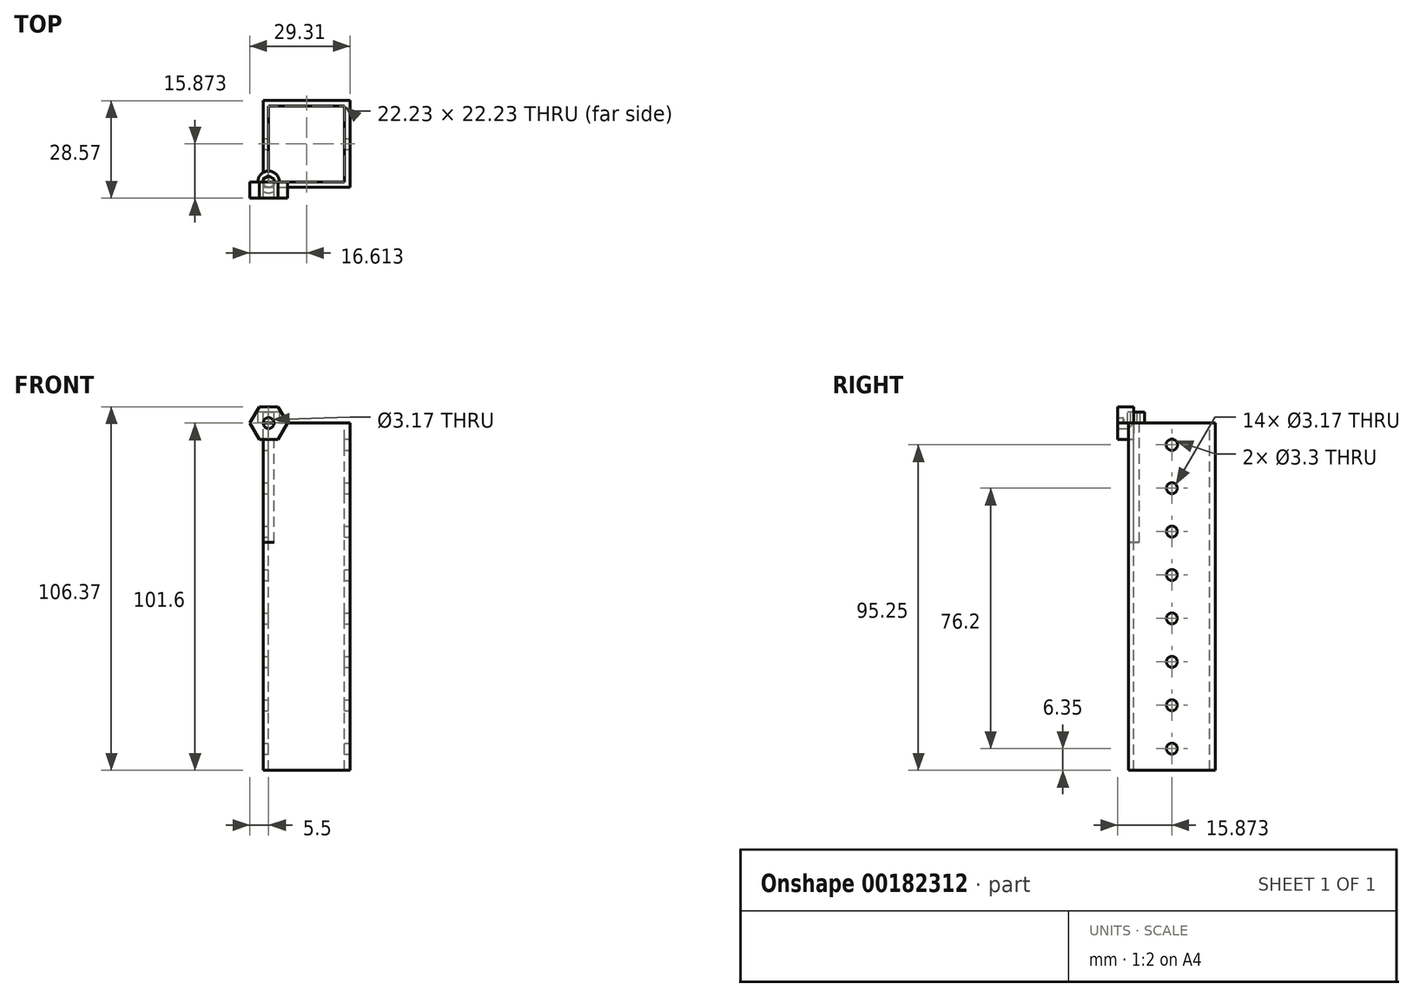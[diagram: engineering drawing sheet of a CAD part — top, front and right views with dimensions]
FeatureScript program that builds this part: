
annotation { "Feature Type Name" : "Feature", "Feature Type Description" : "" }
export const myFeature = defineFeature(function(context is Context, id is Id, definition is map)
    precondition{}
    {
        {
            var Q0;
            Q0=qCreatedBy(makeId("Front.planeOp"),FACE);
            var sketch = newSketch(context, id + "F0", { "sketchPlane" : qUnion([Q0])});
            skCircle(sketch, "E0.cCircle", {"center": v(0, 0) * mm, "radius": 4.76 * mm, "construction": true});
            skLineSegment(sketch, "E0.0", {"start": v(5.5, 0) * mm, "end": v(2.76, -4.76) * mm});
            skLineSegment(sketch, "E0.1", {"start": v(2.76, -4.76) * mm, "end": v(-2.74, -4.77) * mm});
            skLineSegment(sketch, "E0.2", {"start": v(-2.74, -4.77) * mm, "end": v(-5.5, 0) * mm});
            skLineSegment(sketch, "E0.3", {"start": v(-5.5, 0) * mm, "end": v(-2.76, 4.76) * mm});
            skLineSegment(sketch, "E0.4", {"start": v(-2.76, 4.76) * mm, "end": v(2.74, 4.77) * mm});
            skLineSegment(sketch, "E0.5", {"start": v(2.74, 4.77) * mm, "end": v(5.5, 0) * mm});
            skPoint(sketch, "E0.0.midPoint", {"position": v(4.13, -2.38) * mm});
            skSolve(sketch);
        }
        {
            var Q0;
            Q0=makeQuery(id+"F0.imprint","IMPRINT",FACE,{"disambiguationData":[TD([[makeQuery(id+"F0.imprint","IMPRINT",EDGE,{"derivedFrom":sQuery(id+"F0.wireOp",EDGE,"E0.0")}),-1.0]])]});
            var sketch = newSketch(context, id + "F1", { "sketchPlane" : qUnion([Q0])});
            skCircle(sketch, "E1", {"center": v(0, 0) * mm, "radius": 1.58 * mm});
            skSolve(sketch);
        }
        {
            var Q0;
            Q0=makeQuery(id+"F0.imprint","IMPRINT",FACE,{"disambiguationData":[TD([[makeQuery(id+"F0.imprint","IMPRINT",EDGE,{"derivedFrom":sQuery(id+"F0.wireOp",EDGE,"E0.0")}),-1.0]])]});
            extrude(context, id + "F2", {"entities" : qUnion([Q0]), "depth" : 4.76 * mm});
        }
        {
            var Q0;
            Q0 = qSketchRegion(id + "F1", true);
            extrude(context, id + "F3", {"entities" : qUnion([Q0]), "operationType" : NewBodyOperationType.REMOVE, "depth" : 4.76 * mm});
        }
        {
            var Q0;
            Q0=qCreatedBy(makeId("Top.planeOp"),FACE);
            var sketch = newSketch(context, id + "F4", { "sketchPlane" : qUnion([Q0])});
            skCircle(sketch, "E2", {"center": v(0, 0) * mm, "radius": 3.18 * mm});
            skSolve(sketch);
        }
        {
            var Q0;
            Q0=makeQuery(id+"F4.imprint","IMPRINT",FACE,{"disambiguationData":[TD([[makeQuery(id+"F4.imprint","IMPRINT",EDGE,{"derivedFrom":sQuery(id+"F4.wireOp",EDGE,"E2")}),1.0]])]});
            extrude(context, id + "F5", {"entities" : qUnion([Q0]), "depth" : 3.17 * mm});
        }
        {
            var Q0;
            Q0=makeQuery(id+"F5.opExtrude","CAP_FACE",FACE,{"disambiguationData":[OSD([sQuery(id+"F4.wireOp",EDGE,"E2")])],"isStart":true});
            var sketch = newSketch(context, id + "F6", { "sketchPlane" : qUnion([Q0])});
            skCircle(sketch, "E3", {"center": v(0, 0) * mm, "radius": 1.59 * mm});
            skSolve(sketch);
        }
        {
            var Q0;
            Q0=makeQuery(id+"F6.imprint","IMPRINT",FACE,{"disambiguationData":[TD([[makeQuery(id+"F6.imprint","IMPRINT",EDGE,{"derivedFrom":sQuery(id+"F6.wireOp",EDGE,"E3")}),1.0]])]});
            extrude(context, id + "F7", {"entities" : qUnion([Q0]), "operationType" : NewBodyOperationType.ADD, "depth" : 34.92 * mm});
        }
        {
            var Q0;
            Q0=makeQuery(id+"F5.opExtrude","CAP_FACE",FACE,{"disambiguationData":[OSD([sQuery(id+"F4.wireOp",EDGE,"E2")])],"isStart":false});
            var sketch = newSketch(context, id + "F8", { "sketchPlane" : qUnion([Q0])});
            skCircle(sketch, "E4.cCircle", {"center": v(0, 0) * mm, "radius": 1.59 * mm, "construction": true});
            skLineSegment(sketch, "E4.0", {"start": v(-1.59, -0.92) * mm, "end": v(-1.59, 0.92) * mm});
            skLineSegment(sketch, "E4.1", {"start": v(-1.59, 0.92) * mm, "end": v(0, 1.83) * mm});
            skLineSegment(sketch, "E4.2", {"start": v(0, 1.83) * mm, "end": v(1.59, 0.92) * mm});
            skLineSegment(sketch, "E4.3", {"start": v(1.59, 0.92) * mm, "end": v(1.59, -0.92) * mm});
            skLineSegment(sketch, "E4.4", {"start": v(1.59, -0.92) * mm, "end": v(0, -1.83) * mm});
            skLineSegment(sketch, "E4.5", {"start": v(0, -1.83) * mm, "end": v(-1.59, -0.92) * mm});
            skPoint(sketch, "E4.0.midPoint", {"position": v(-1.59, 0) * mm});
            skSolve(sketch);
        }
        {
            var Q0;
            Q0=makeQuery(id+"F8.imprint","IMPRINT",FACE,{"disambiguationData":[TD([[makeQuery(id+"F8.imprint","IMPRINT",EDGE,{"derivedFrom":sQuery(id+"F8.wireOp",EDGE,"E4.0")}),-1.0]])]});
            extrude(context, id + "F9", {"entities" : qUnion([Q0]), "operationType" : NewBodyOperationType.REMOVE, "oppositeDirection" : true, "depth" : 3.15 * mm});
        }
        {
            var Q0;
            Q0=qCreatedBy(makeId("Top.planeOp"),FACE);
            var sketch = newSketch(context, id + "F10", { "sketchPlane" : qUnion([Q0])});
            skLineSegment(sketch, "E5.bottom", {"start": v(0, 0) * mm, "end": v(22.23, 0) * mm});
            skLineSegment(sketch, "E5.top", {"start": v(0, 22.23) * mm, "end": v(22.22, 22.23) * mm});
            skLineSegment(sketch, "E5.left", {"start": v(0, 0) * mm, "end": v(0, 22.23) * mm});
            skLineSegment(sketch, "E5.right", {"start": v(22.23, 0) * mm, "end": v(22.23, 22.23) * mm});
            skSolve(sketch);
        }
        {
            var Q0;
            Q0=qCreatedBy(makeId("Top.planeOp"),FACE);
            var sketch = newSketch(context, id + "F11", { "sketchPlane" : qUnion([Q0])});
            skLineSegment(sketch, "E6.bottom", {"start": v(-1.59, -1.59) * mm, "end": v(23.81, -1.59) * mm});
            skLineSegment(sketch, "E6.top", {"start": v(-1.59, 23.81) * mm, "end": v(23.81, 23.81) * mm});
            skLineSegment(sketch, "E6.left", {"start": v(-1.59, -1.59) * mm, "end": v(-1.59, 23.81) * mm});
            skLineSegment(sketch, "E6.right", {"start": v(23.81, -1.59) * mm, "end": v(23.81, 23.81) * mm});
            skSolve(sketch);
        }
        {
            var Q0;
            Q0=makeQuery(id+"F11.imprint","IMPRINT",FACE,{"disambiguationData":[TD([[makeQuery(id+"F11.imprint","IMPRINT",EDGE,{"derivedFrom":sQuery(id+"F11.wireOp",EDGE,"E6.bottom")}),1.0]])]});
            extrude(context, id + "F12", {"entities" : qUnion([Q0]), "oppositeDirection" : true, "depth" : 101.6 * mm});
        }
        {
            var Q0;
            Q0=makeQuery(id+"F10.imprint","IMPRINT",FACE,{"disambiguationData":[TD([[makeQuery(id+"F10.imprint","IMPRINT",EDGE,{"derivedFrom":sQuery(id+"F10.wireOp",EDGE,"E5.bottom")}),1.0]])]});
            extrude(context, id + "F13", {"entities" : qUnion([Q0]), "operationType" : NewBodyOperationType.REMOVE, "oppositeDirection" : true, "depth" : 101.6 * mm});
        }
        {
            var Q0;
            Q0=makeQuery(id+"F12.opExtrude","SWEPT_FACE",FACE,{"disambiguationData":[OSD([sQuery(id+"F11.wireOp",EDGE,"E6.right")])]});
            var sketch = newSketch(context, id + "F14", { "sketchPlane" : qUnion([Q0])});
            skCircle(sketch, "E7", {"center": v(11.11, -6.35) * mm, "radius": 1.65 * mm});
            skSolve(sketch);
        }
        {
            var Q0;
            Q0=makeQuery(id+"F14.imprint","IMPRINT",FACE,{"disambiguationData":[TD([[makeQuery(id+"F14.imprint","IMPRINT",EDGE,{"derivedFrom":sQuery(id+"F14.wireOp",EDGE,"E7")}),-1.0]])]});
            var sketch = newSketch(context, id + "F15", { "sketchPlane" : qUnion([Q0])});
            skCircle(sketch, "E8", {"center": v(11.11, -19.05) * mm, "radius": 1.59 * mm});
            skSolve(sketch);
        }
        {
            var Q0;
            Q0=makeQuery(id+"F14.imprint","IMPRINT",FACE,{"disambiguationData":[TD([[makeQuery(id+"F14.imprint","IMPRINT",EDGE,{"derivedFrom":sQuery(id+"F14.wireOp",EDGE,"E7")}),-1.0]])]});
            var sketch = newSketch(context, id + "F16", { "sketchPlane" : qUnion([Q0])});
            skCircle(sketch, "E9", {"center": v(11.11, -31.75) * mm, "radius": 1.59 * mm});
            skSolve(sketch);
        }
        {
            var Q0;
            Q0=makeQuery(id+"F14.imprint","IMPRINT",FACE,{"disambiguationData":[TD([[makeQuery(id+"F14.imprint","IMPRINT",EDGE,{"derivedFrom":sQuery(id+"F14.wireOp",EDGE,"E7")}),-1.0]])]});
            var sketch = newSketch(context, id + "F17", { "sketchPlane" : qUnion([Q0])});
            skCircle(sketch, "E10", {"center": v(11.11, -44.45) * mm, "radius": 1.59 * mm});
            skSolve(sketch);
        }
        {
            var Q0;
            Q0=makeQuery(id+"F14.imprint","IMPRINT",FACE,{"disambiguationData":[TD([[makeQuery(id+"F14.imprint","IMPRINT",EDGE,{"derivedFrom":sQuery(id+"F14.wireOp",EDGE,"E7")}),-1.0]])]});
            var sketch = newSketch(context, id + "F18", { "sketchPlane" : qUnion([Q0])});
            skCircle(sketch, "E11", {"center": v(11.11, -57.15) * mm, "radius": 1.59 * mm});
            skSolve(sketch);
        }
        {
            var Q0;
            Q0=makeQuery(id+"F14.imprint","IMPRINT",FACE,{"disambiguationData":[TD([[makeQuery(id+"F14.imprint","IMPRINT",EDGE,{"derivedFrom":sQuery(id+"F14.wireOp",EDGE,"E7")}),-1.0]])]});
            var sketch = newSketch(context, id + "F19", { "sketchPlane" : qUnion([Q0])});
            skCircle(sketch, "E12", {"center": v(11.11, -69.85) * mm, "radius": 1.59 * mm});
            skSolve(sketch);
        }
        {
            var Q0;
            Q0=makeQuery(id+"F14.imprint","IMPRINT",FACE,{"disambiguationData":[TD([[makeQuery(id+"F14.imprint","IMPRINT",EDGE,{"derivedFrom":sQuery(id+"F14.wireOp",EDGE,"E7")}),-1.0]])]});
            var sketch = newSketch(context, id + "F20", { "sketchPlane" : qUnion([Q0])});
            skCircle(sketch, "E13", {"center": v(11.11, -82.55) * mm, "radius": 1.59 * mm});
            skSolve(sketch);
        }
        {
            var Q0;
            Q0=makeQuery(id+"F14.imprint","IMPRINT",FACE,{"disambiguationData":[TD([[makeQuery(id+"F14.imprint","IMPRINT",EDGE,{"derivedFrom":sQuery(id+"F14.wireOp",EDGE,"E7")}),-1.0]])]});
            var sketch = newSketch(context, id + "F21", { "sketchPlane" : qUnion([Q0])});
            skCircle(sketch, "E14", {"center": v(11.11, -95.25) * mm, "radius": 1.59 * mm});
            skSolve(sketch);
        }
        {
            var Q0;
            Q0=makeQuery(id+"F14.imprint","IMPRINT",FACE,{"disambiguationData":[TD([[makeQuery(id+"F14.imprint","IMPRINT",EDGE,{"derivedFrom":sQuery(id+"F14.wireOp",EDGE,"E7")}),1.0]])]});
            extrude(context, id + "F22", {"entities" : qUnion([Q0]), "operationType" : NewBodyOperationType.REMOVE, "oppositeDirection" : true, "depth" : 25.4 * mm});
        }
        {
            var Q0;
            Q0=makeQuery(id+"F15.imprint","IMPRINT",FACE,{"disambiguationData":[TD([[makeQuery(id+"F15.imprint","IMPRINT",EDGE,{"derivedFrom":sQuery(id+"F15.wireOp",EDGE,"E8")}),1.0]])]});
            extrude(context, id + "F23", {"entities" : qUnion([Q0]), "operationType" : NewBodyOperationType.REMOVE, "oppositeDirection" : true, "depth" : 25.4 * mm});
        }
        {
            var Q0;
            Q0 = qSketchRegion(id + "F21", true);
            extrude(context, id + "F24", {"entities" : qUnion([Q0]), "operationType" : NewBodyOperationType.REMOVE, "oppositeDirection" : true, "depth" : 25.4 * mm});
        }
        {
            var Q0;
            Q0 = qSketchRegion(id + "F20", true);
            extrude(context, id + "F25", {"entities" : qUnion([Q0]), "operationType" : NewBodyOperationType.REMOVE, "oppositeDirection" : true, "depth" : 25.4 * mm});
        }
        {
            var Q0;
            Q0 = qSketchRegion(id + "F19", true);
            extrude(context, id + "F26", {"entities" : qUnion([Q0]), "operationType" : NewBodyOperationType.REMOVE, "oppositeDirection" : true, "depth" : 25.4 * mm});
        }
        {
            var Q0;
            Q0 = qSketchRegion(id + "F18", true);
            extrude(context, id + "F27", {"entities" : qUnion([Q0]), "operationType" : NewBodyOperationType.REMOVE, "oppositeDirection" : true, "depth" : 25.4 * mm});
        }
        {
            var Q0;
            Q0 = qSketchRegion(id + "F17", true);
            extrude(context, id + "F28", {"entities" : qUnion([Q0]), "operationType" : NewBodyOperationType.REMOVE, "oppositeDirection" : true, "depth" : 25.4 * mm});
        }
        {
            var Q0;
            Q0 = qSketchRegion(id + "F16", true);
            extrude(context, id + "F29", {"entities" : qUnion([Q0]), "operationType" : NewBodyOperationType.REMOVE, "oppositeDirection" : true, "depth" : 25.4 * mm});
        }
    });
